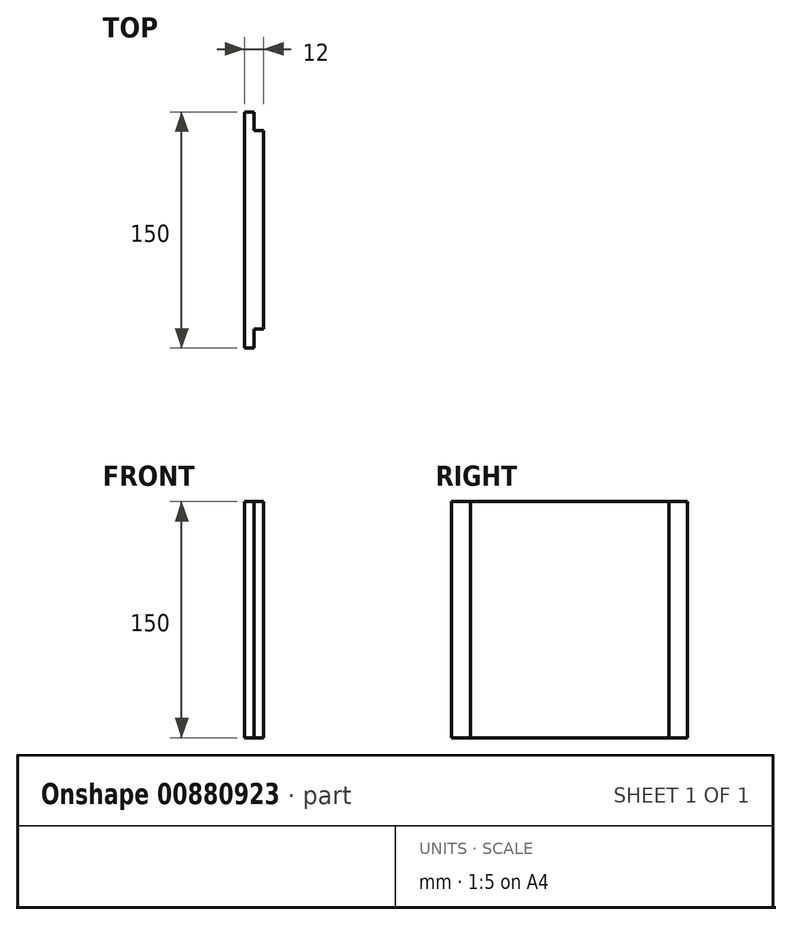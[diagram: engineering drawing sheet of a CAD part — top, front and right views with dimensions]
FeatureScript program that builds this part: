
annotation { "Feature Type Name" : "Feature", "Feature Type Description" : "" }
export const myFeature = defineFeature(function(context is Context, id is Id, definition is map)
    precondition{}
    {
        {
            var Q0;
            Q0=qCreatedBy(makeId("Top.planeOp"),FACE);
            var sketch = newSketch(context, id + "F0", { "sketchPlane" : qUnion([Q0])});
            skLineSegment(sketch, "E0.bottom", {"start": v(-6, 75) * mm, "end": v(0, 75) * mm});
            skLineSegment(sketch, "E0.top", {"start": v(-6, -75) * mm, "end": v(0, -75) * mm});
            skLineSegment(sketch, "E0.left", {"start": v(-6, 75) * mm, "end": v(-6, -75) * mm});
            skLineSegment(sketch, "E0.right", {"start": v(6, 63) * mm, "end": v(6, -63) * mm});
            skPoint(sketch, "E0.middle", {"position": v(0, 0) * mm});
            skLineSegment(sketch, "E1.bottom", {"start": v(0, 75) * mm, "end": v(0, 75) * mm});
            skLineSegment(sketch, "E1.top", {"start": v(0, 75) * mm, "end": v(0, 75) * mm});
            skLineSegment(sketch, "E1.left", {"start": v(0, 75) * mm, "end": v(0, 75) * mm});
            skLineSegment(sketch, "E1.right", {"start": v(0, 75) * mm, "end": v(0, 75) * mm});
            skPoint(sketch, "E1.middle", {"position": v(0, 75) * mm});
            skPoint(sketch, "E1.cornerSnap0", {"position": v(0, 75) * mm});
            skLineSegment(sketch, "E2", {"start": v(0, 75) * mm, "end": v(0, 63) * mm});
            skLineSegment(sketch, "E3", {"start": v(0, 63) * mm, "end": v(6, 63) * mm});
            skPoint(sketch, "E4.orphan", {"position": v(6, 75) * mm});
            skLineSegment(sketch, "E5", {"start": v(0, -75) * mm, "end": v(0, -63) * mm});
            skLineSegment(sketch, "E6", {"start": v(0, -63) * mm, "end": v(6, -63) * mm});
            skPoint(sketch, "E7.orphan", {"position": v(6, -75) * mm});
            skSolve(sketch);
        }
        {
            var Q0;
            Q0 = qSketchRegion(id + "F0", true);
            extrude(context, id + "F1", {"entities" : qUnion([Q0]), "endBound" : BoundingType.SYMMETRIC, "depth" : 150 * mm, "offsetDistance" : 25 * mm});
        }
    });
